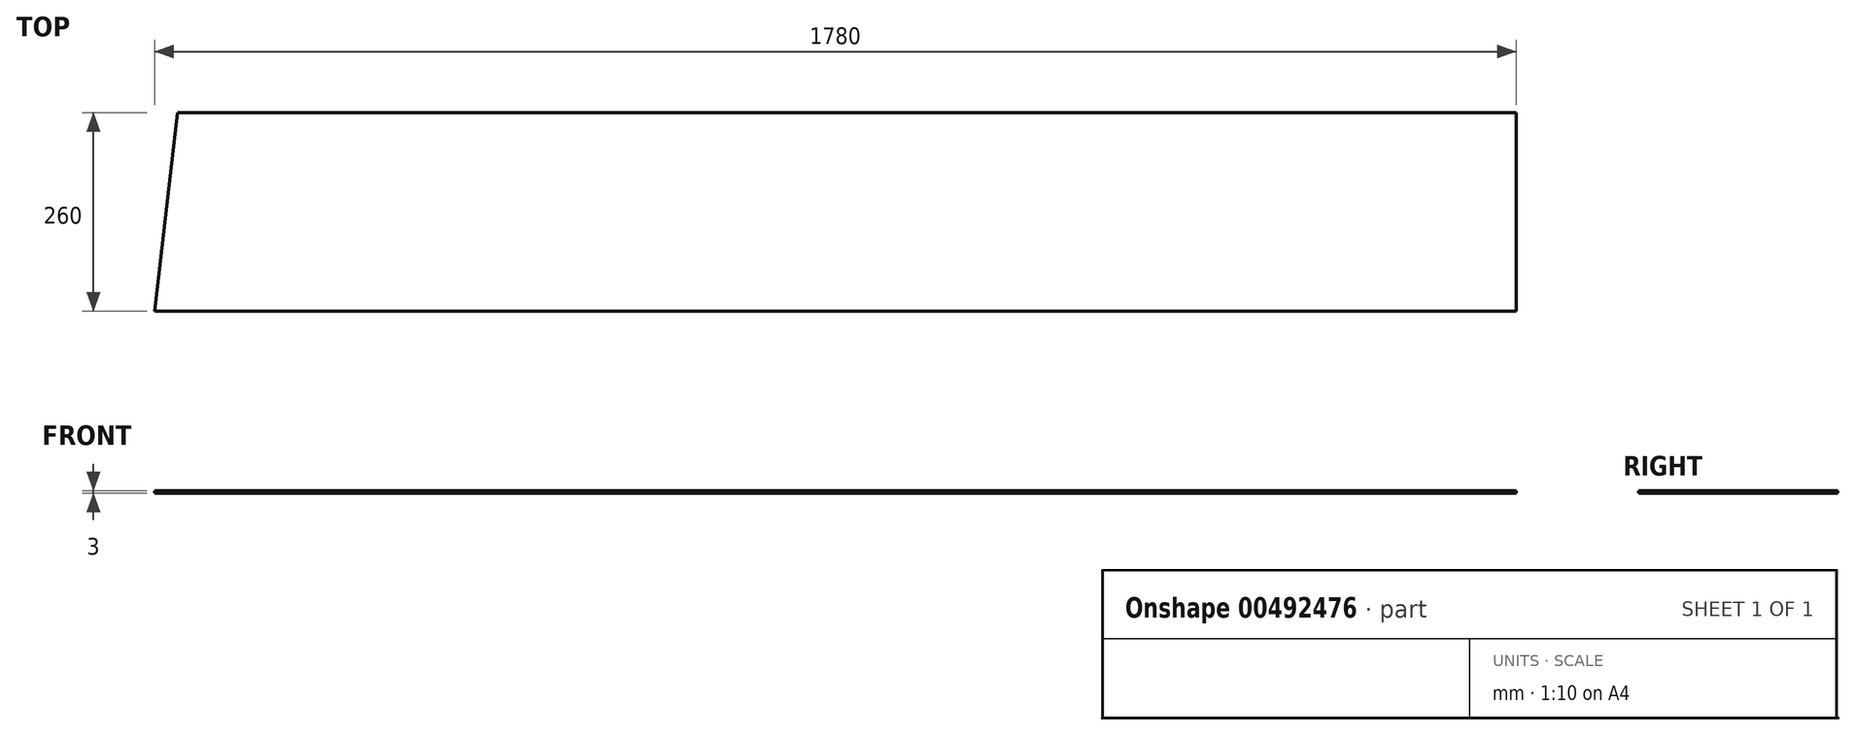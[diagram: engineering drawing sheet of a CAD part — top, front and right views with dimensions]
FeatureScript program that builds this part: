
annotation { "Feature Type Name" : "Feature", "Feature Type Description" : "" }
export const myFeature = defineFeature(function(context is Context, id is Id, definition is map)
    precondition{}
    {
        {
            var Q0;
            Q0=qCreatedBy(makeId("Top.planeOp"),FACE);
            var sketch = newSketch(context, id + "F0", { "sketchPlane" : qUnion([Q0])});
            skLineSegment(sketch, "E0", {"start": v(-812.2, -260) * mm, "end": v(967.8, -260) * mm});
            skLineSegment(sketch, "E1", {"start": v(967.8, -260) * mm, "end": v(967.8, 0) * mm});
            skLineSegment(sketch, "E2", {"start": v(967.8, 0) * mm, "end": v(-782.2, 0) * mm});
            skLineSegment(sketch, "E3", {"start": v(-782.2, 0) * mm, "end": v(-812.2, -260) * mm});
            skLineSegment(sketch, "E4", {"start": v(967.8, -40) * mm, "end": v(-786.81, -40) * mm, "construction": true});
            skLineSegment(sketch, "E5", {"start": v(967.8, -170) * mm, "end": v(-801.81, -170) * mm, "construction": true});
            skSolve(sketch);
        }
        {
            var Q0;
            Q0=makeQuery(id+"F0.imprint","IMPRINT",FACE,{"disambiguationData":[TD([[makeQuery(id+"F0.imprint","IMPRINT",EDGE,{"derivedFrom":sQuery(id+"F0.wireOp",EDGE,"E0")}),1.0]])]});
            extrude(context, id + "F1", {"entities" : qUnion([Q0]), "depth" : 3 * mm});
        }
    });
